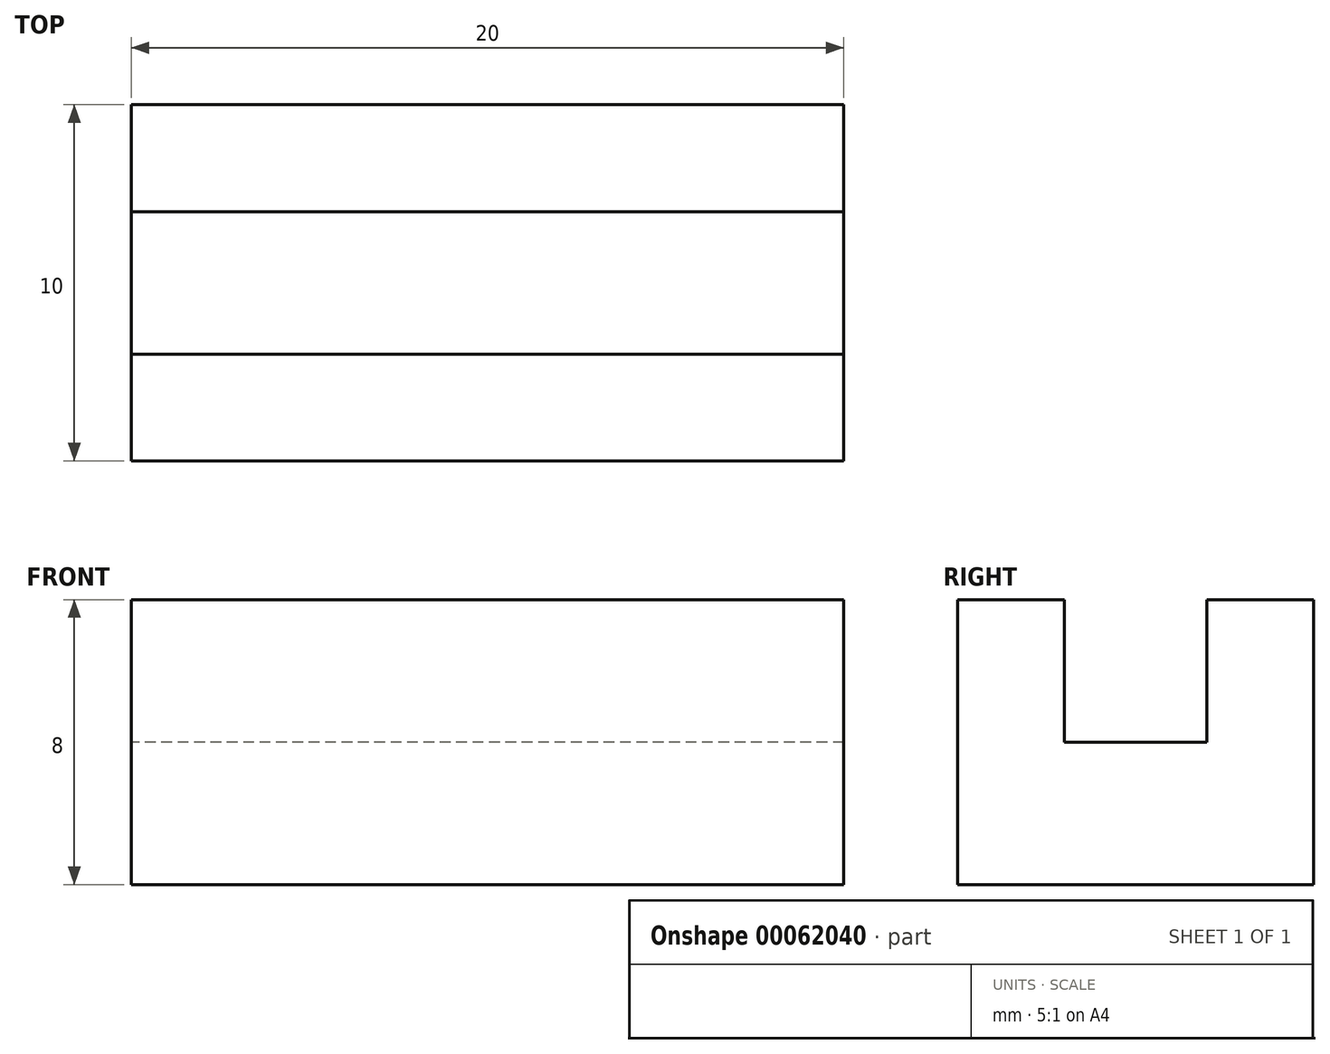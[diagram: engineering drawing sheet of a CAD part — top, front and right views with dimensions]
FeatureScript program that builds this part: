
annotation { "Feature Type Name" : "Feature", "Feature Type Description" : "" }
export const myFeature = defineFeature(function(context is Context, id is Id, definition is map)
    precondition{}
    {
        {
            var Q0;
            Q0=qCreatedBy(makeId("Top.planeOp"),FACE);
            var sketch = newSketch(context, id + "F0", { "sketchPlane" : qUnion([Q0])});
            skLineSegment(sketch, "E0.bottom", {"start": v(-9.03, 6.73) * mm, "end": v(10.97, 6.73) * mm});
            skLineSegment(sketch, "E0.top", {"start": v(-9.03, -3.27) * mm, "end": v(10.97, -3.27) * mm});
            skLineSegment(sketch, "E0.left", {"start": v(-9.03, 6.73) * mm, "end": v(-9.03, -3.27) * mm});
            skLineSegment(sketch, "E0.right", {"start": v(10.97, 6.73) * mm, "end": v(10.97, -3.27) * mm});
            skSolve(sketch);
        }
        {
            var Q0;
            Q0 = qSketchRegion(id + "F0", true);
            extrude(context, id + "F1", {"entities" : qUnion([Q0]), "depth" : 8 * mm});
        }
        {
            var Q0;
            Q0=makeQuery(id+"F1.opExtrude","SWEPT_FACE",FACE,{"disambiguationData":[OSD([sQuery(id+"F0.wireOp",EDGE,"E0.left")])]});
            var sketch = newSketch(context, id + "F2", { "sketchPlane" : qUnion([Q0])});
            skLineSegment(sketch, "E1", {"start": v(-3.73, 8) * mm, "end": v(-3.73, 4) * mm});
            skLineSegment(sketch, "E2", {"start": v(-3.73, 4) * mm, "end": v(0.27, 4) * mm});
            skLineSegment(sketch, "E3", {"start": v(0.27, 4) * mm, "end": v(0.27, 8) * mm});
            skLineSegment(sketch, "E4", {"start": v(-1.73, 8) * mm, "end": v(-1.73, 4) * mm, "construction": true});
            skSolve(sketch);
        }
        {
            var Q0;
            {var subQ0=sQuery(id+"F2.wireOp",EDGE,"E1");Q0=makeQuery(id+"F2.imprint","IMPRINT",FACE,{"disambiguationData":[TD([[makeQuery(id+"F2.imprint","IMPRINT",EDGE,{"derivedFrom":subQ0}),1.0]])]});}
            extrude(context, id + "F3", {"entities" : qUnion([Q0]), "operationType" : NewBodyOperationType.REMOVE, "oppositeDirection" : true, "depth" : 25 * mm});
        }
    });
